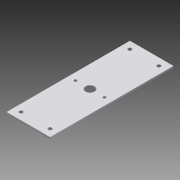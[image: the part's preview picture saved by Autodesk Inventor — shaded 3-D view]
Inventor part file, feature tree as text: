
AUTODESK INVENTOR PART (.ipt)
format: ipt  version: 2015 SP1 (Build 190203100, 203)  size: 121,856 bytes
history: native  units: in
note: dims shown in document units (in); Inventor stores cm internally (conversion verified against a paired STEP export)
features: sketch x3, extrude x2, hole x1
ambient origin geometry x8: Origin, YZ Plane, XZ Plane, XY Plane, X Axis, Y Axis, Z Axis, Center Point
bodies: Solid1 (feature_tree)
feature tree (6):
  extrude  "Extrusion1"  Depth=8.5in
  extrude  "Extrusion2"  Depth=0.125in
  hole  "Hole1"  [1 undecoded]
  sketch  "Sketch1"  dims[d0=3.0in d1=8.5in]
  sketch  "Sketch2"  dims[d2=0.125in d3=0.0in d4=4.25in]
  sketch  "Sketch3"  dims[d5=1.5in d6=1.0in d7=1.0in d8=4.25in d9=4.25in d10=0.2in d11=0.2in d12=0.625in d13=1.0in d14=0.0in d15=0.5in d16=0.5in d17=0.5in d18=0.5in d19=0.5in d20=0.5in d21=0.5in d22=0.5in d23=0.25in d24=0.75in d25=0.375in d26=0.25in d27=0.5635in d28=1.0in d29=0.8108in]
note: 1 required parameter value undecoded (feature->parameter linkage not recoverable at this tier; creation-order binding heuristic only, values carry confidence <= 0.55)
